annotation { "Feature Type Name" : "Feature", "Feature Type Description" : "" }
export const myFeature = defineFeature(function(context is Context, id is Id, definition is map)
    precondition{}
    {
        {
            var Q0;
            Q0=qCreatedBy(makeId("Front.planeOp"),FACE);
            var sketch = newSketch(context, id + "F0", { "sketchPlane" : qUnion([Q0])});
            skLineSegment(sketch, "E0.bottom", {"start": v(-24.45, 49.17) * mm, "end": v(75.55, 49.17) * mm});
            skLineSegment(sketch, "E0.top", {"start": v(-24.45, 19.17) * mm, "end": v(75.55, 19.17) * mm});
            skLineSegment(sketch, "E0.left", {"start": v(-24.45, 49.17) * mm, "end": v(-24.45, 19.17) * mm});
            skLineSegment(sketch, "E0.right", {"start": v(75.55, 49.17) * mm, "end": v(75.55, 19.17) * mm});
            skArc(sketch, "E1", {"start": v(58.23, 49.17) * mm, "mid": v(25.55, 71.65) * mm, "end": v(-7.13, 49.17) * mm});
            skCircle(sketch, "E2", {"center": v(25.55, 69.17) * mm, "radius": 1.5 * mm});
            skPoint(sketch, "E3", {"position": v(25.55, 49.17) * mm});
            skText(sketch, "E4", { "text": "Lars Larsen\n", "fontName": "AllertaStencil-Regular.ttf"});
            const initialGuessF0  = {"E4": [-0.02195, 0.03228, 1, 0, 0.01189]};
            skSetInitialGuess(sketch, initialGuessF0);
            skSolve(sketch);
        }
        {
            var Q0;
            {var subQ0=sQuery(id+"F0.wireOp",EDGE,"E1");Q0=makeQuery(id+"F0.imprint","IMPRINT",FACE,{"disambiguationData":[TD([[makeQuery(id+"F0.imprint","IMPRINT",EDGE,{"derivedFrom":subQ0}),1.0]])]});}
            var Q1;
            Q1=makeQuery(id+"F0.imprint","IMPRINT",FACE,{"disambiguationData":[TD([[makeQuery(id+"F0.imprint","IMPRINT",EDGE,{"derivedFrom":sQuery(id+"F0.wireOp",EDGE,"E0.top")}),1.0]])]});
            extrude(context, id + "F1", {"entities" : qUnion([Q0, Q1]), "depth" : 3 * mm});
        }
    });